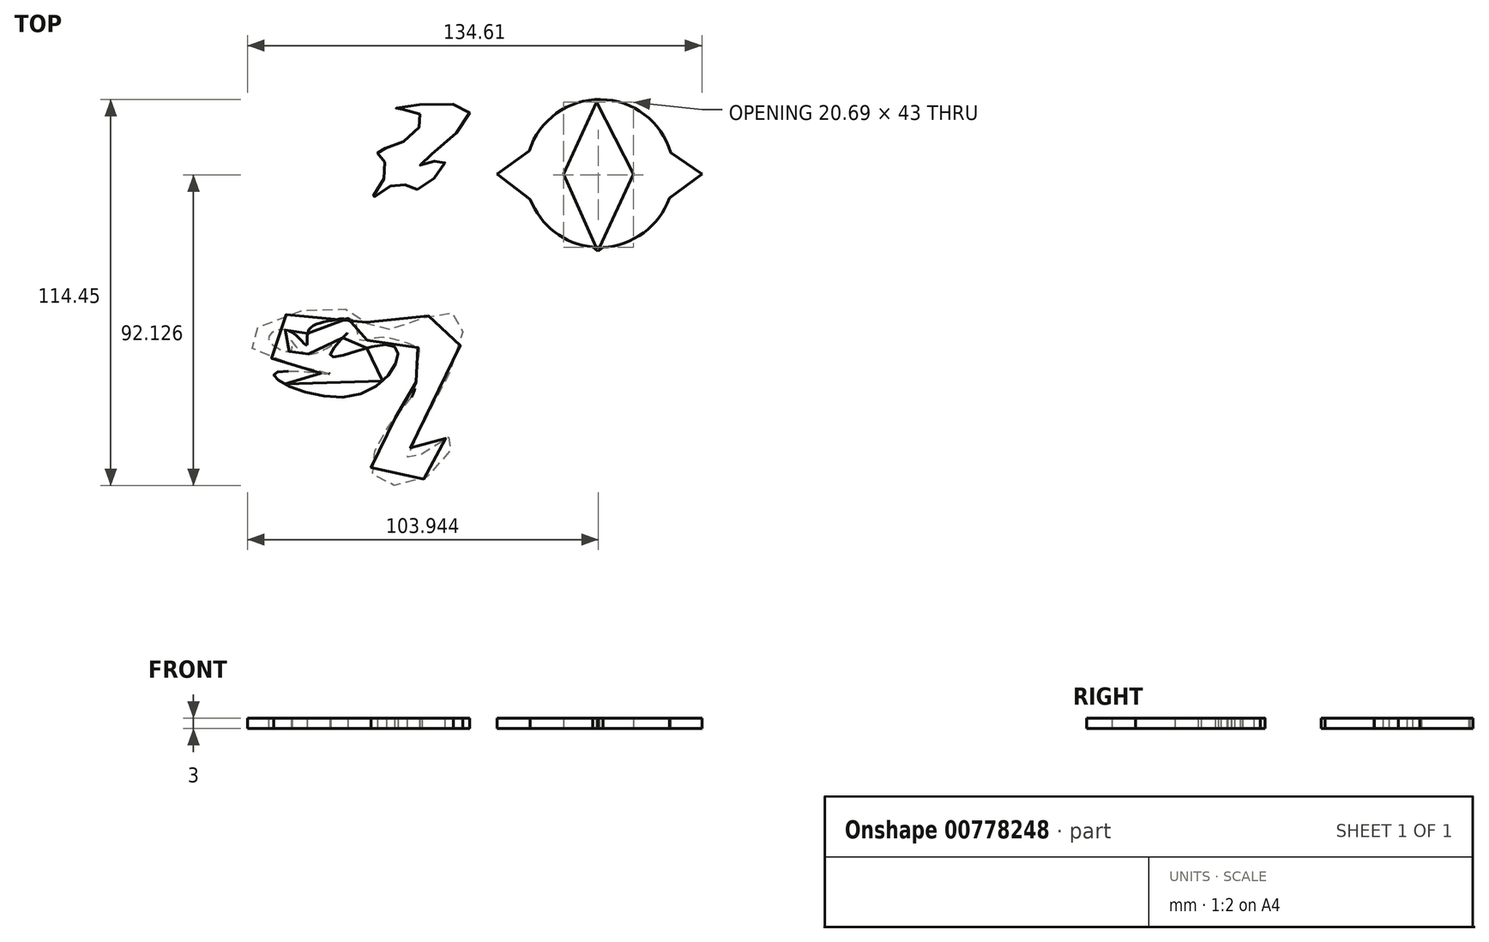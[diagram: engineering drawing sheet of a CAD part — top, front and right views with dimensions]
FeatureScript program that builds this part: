
annotation { "Feature Type Name" : "Feature", "Feature Type Description" : "" }
export const myFeature = defineFeature(function(context is Context, id is Id, definition is map)
    precondition{}
    {
        {
            var Q0;
            Q0=qCreatedBy(makeId("Top.planeOp"),FACE);
            var sketch = newSketch(context, id + "F0", { "sketchPlane" : qUnion([Q0])});
            skFitSpline(sketch, "E0", {"points": [v(-20.18, 50.94) * mm, v(-25.34, 42.58) * mm, v(-32.8, 39.56) * mm, v(-30.14, 34.76) * mm, v(-34.58, 25.87) * mm, v(-26.76, 30.31) * mm, v(-20.54, 28.71) * mm, v(-13.07, 37.25) * mm, v(-20.18, 35.83) * mm, v(-5.6, 51.83) * mm, v(-27.65, 52.54) * mm, v(-20.18, 50.94) * mm]});
            skSolve(sketch);
        }
        {
            var Q0;
            Q0 = qSketchRegion(id + "F0", true);
            extrude(context, id + "F1", {"entities" : qUnion([Q0]), "depth" : 3 * mm, "offsetDistance" : 25 * mm});
        }
        {
            var Q0;
            Q0=qCreatedBy(makeId("Top.planeOp"),FACE);
            var sketch = newSketch(context, id + "F2", { "sketchPlane" : qUnion([Q0])});
            skFitSpline(sketch, "E1", {"points": [v(-53.29, -20.21) * mm, v(-41.56, -13.74) * mm, v(-46.81, -20.74) * mm, v(-28.09, -17.76) * mm, v(-38.41, -32.29) * mm, v(-63.26, -25.81) * mm, v(-46.64, -26.16) * mm, v(-71.14, -17.06) * mm, v(-43.66, -6.56) * mm, v(-32.11, -13.04) * mm, v(-11.81, -7.79) * mm, v(-8.31, -17.76) * mm, v(-23.71, -51.71) * mm, v(-10.94, -44.71) * mm, v(-17.76, -56.44) * mm, v(-33.86, -56.44) * mm, v(-31.76, -45.24) * mm, v(-25.46, -36.49) * mm, v(-22.14, -31.76) * mm, v(-20.74, -22.31) * mm, v(-20.39, -18.46) * mm, v(-20.74, -18.29) * mm, v(-31.59, -15.31) * mm, v(-38.06, -16.01) * mm, v(-39.46, -10.59) * mm, v(-46.29, -10.24) * mm, v(-53.29, -13.39) * mm, v(-53.81, -17.59) * mm, v(-59.41, -13.21) * mm, v(-65.01, -15.84) * mm, v(-58.36, -19.16) * mm, v(-58.36, -16.19) * mm, v(-53.29, -20.21) * mm]});
            skSolve(sketch);
        }
        {
            var Q0;
            Q0 = qSketchRegion(id + "F2", true);
            extrude(context, id + "F3", {"entities" : qUnion([Q0]), "depth" : 3 * mm, "offsetDistance" : 25 * mm});
        }
        {
            var Q0;
            Q0=qCreatedBy(makeId("Top.planeOp"),FACE);
            var sketch = newSketch(context, id + "F4", { "sketchPlane" : qUnion([Q0])});
            skLineSegment(sketch, "E2", {"start": v(32.08, 54.43) * mm, "end": v(22.28, 33.2) * mm});
            skLineSegment(sketch, "E3", {"start": v(22.28, 33.2) * mm, "end": v(32.44, 10.33) * mm});
            skLineSegment(sketch, "E4", {"start": v(32.44, 10.33) * mm, "end": v(42.97, 33.2) * mm});
            skLineSegment(sketch, "E5", {"start": v(42.97, 33.2) * mm, "end": v(32.08, 54.43) * mm});
            skLineSegment(sketch, "E6", {"start": v(42.97, 33.2) * mm, "end": v(63.3, 33.2) * mm});
            skLineSegment(sketch, "E7", {"start": v(22.28, 33.2) * mm, "end": v(2.68, 33.2) * mm});
            skLineSegment(sketch, "E8", {"start": v(2.68, 33.2) * mm, "end": v(32.44, 10.33) * mm});
            skLineSegment(sketch, "E9", {"start": v(63.3, 33.2) * mm, "end": v(32.08, 54.43) * mm});
            skLineSegment(sketch, "E10", {"start": v(63.3, 33.2) * mm, "end": v(32.44, 10.33) * mm});
            skLineSegment(sketch, "E11", {"start": v(2.68, 33.2) * mm, "end": v(32.08, 54.43) * mm});
            skCircle(sketch, "E12", {"center": v(32.99, 33.34) * mm, "radius": 21.91 * mm});
            skSolve(sketch);
        }
        {
            var Q0;
            Q0 = qSketchRegion(id + "F4", true);
            extrude(context, id + "F5", {"entities" : qUnion([Q0]), "depth" : 3 * mm, "offsetDistance" : 25 * mm});
        }
    });
